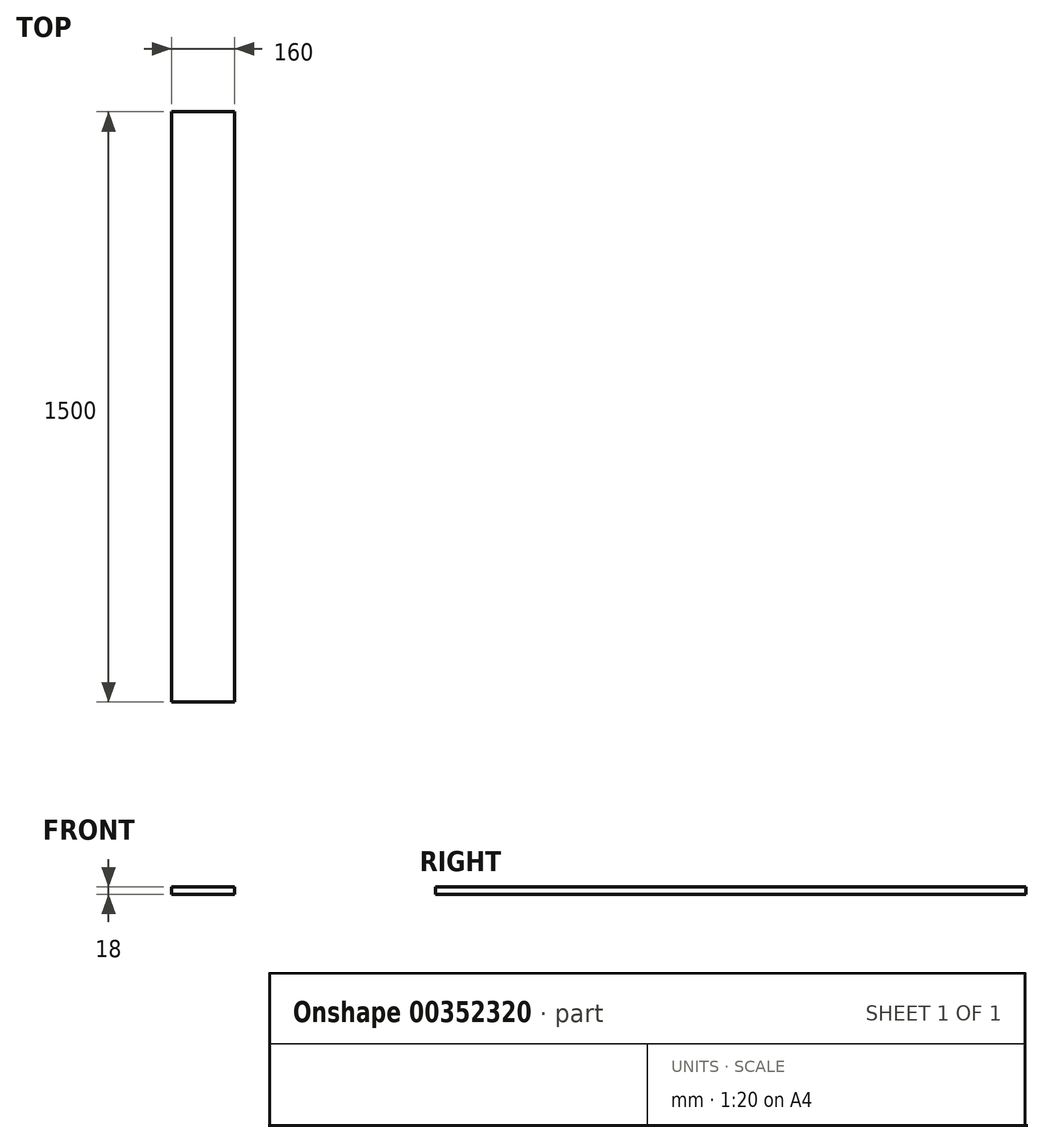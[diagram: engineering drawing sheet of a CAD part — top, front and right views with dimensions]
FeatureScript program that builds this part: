
annotation { "Feature Type Name" : "Feature", "Feature Type Description" : "" }
export const myFeature = defineFeature(function(context is Context, id is Id, definition is map)
    precondition{}
    {
        {
            var Q0;
            Q0=qCreatedBy(makeId("Front.planeOp"),FACE);
            var sketch = newSketch(context, id + "F0", { "sketchPlane" : qUnion([Q0])});
            skLineSegment(sketch, "E0.bottom", {"start": v(0, 0) * mm, "end": v(160, 0) * mm});
            skLineSegment(sketch, "E0.top", {"start": v(0, 18) * mm, "end": v(160, 18) * mm});
            skLineSegment(sketch, "E0.left", {"start": v(0, 0) * mm, "end": v(0, 18) * mm});
            skLineSegment(sketch, "E0.right", {"start": v(160, 0) * mm, "end": v(160, 18) * mm});
            skSolve(sketch);
        }
        {
            var Q0;
            Q0=makeQuery(id+"F0.imprint","IMPRINT",FACE,{"disambiguationData":[TD([[makeQuery(id+"F0.imprint","IMPRINT",EDGE,{"derivedFrom":sQuery(id+"F0.wireOp",EDGE,"E0.bottom")}),1.0]])]});
            extrude(context, id + "F1", {"entities" : qUnion([Q0]), "depth" : 1500 * mm});
        }
    });
